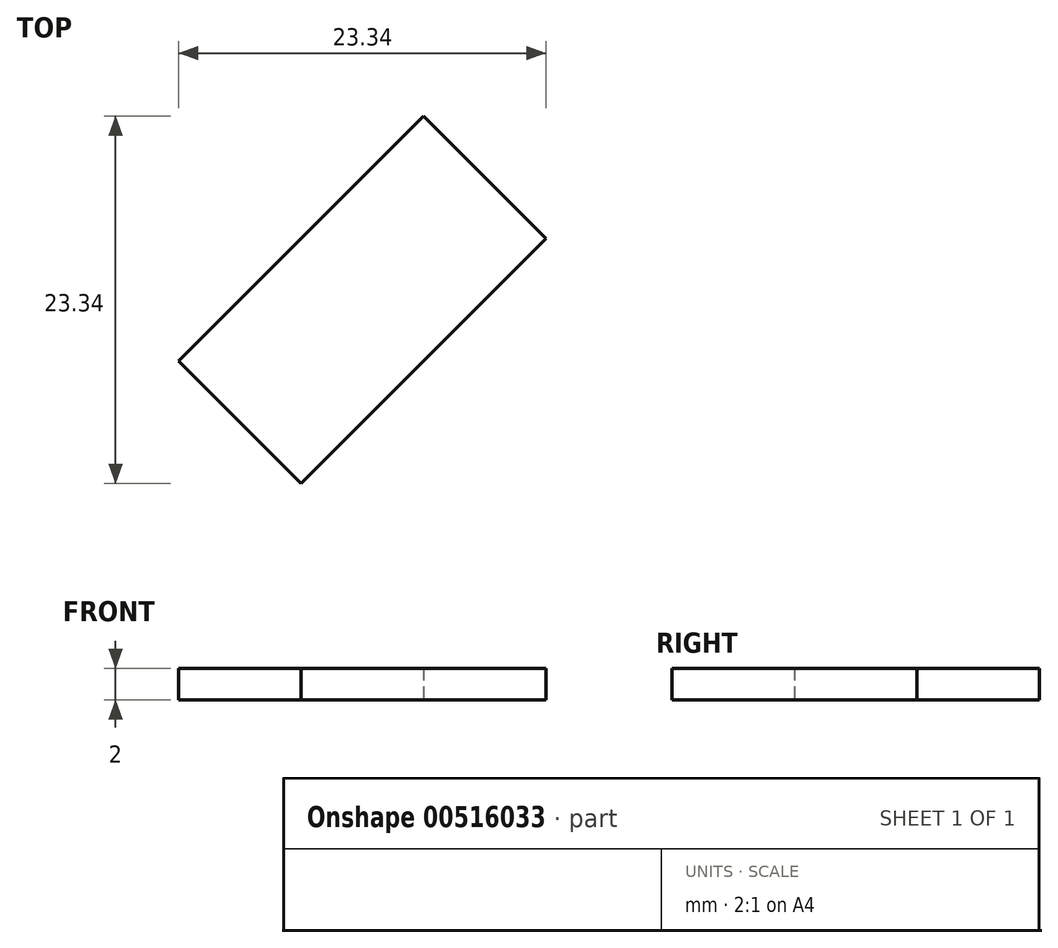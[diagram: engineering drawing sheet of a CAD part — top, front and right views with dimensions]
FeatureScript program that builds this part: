
annotation { "Feature Type Name" : "Feature", "Feature Type Description" : "" }
export const myFeature = defineFeature(function(context is Context, id is Id, definition is map)
    precondition{}
    {
        {
            var Q0;
            Q0=qCreatedBy(makeId("Top.planeOp"),FACE);
            var sketch = newSketch(context, id + "F0", { "sketchPlane" : qUnion([Q0])});
            skLineSegment(sketch, "E0", {"start": v(-7.78, 0) * mm, "end": v(0, -7.78) * mm});
            skLineSegment(sketch, "E1", {"start": v(0, -7.78) * mm, "end": v(15.56, 7.78) * mm});
            skLineSegment(sketch, "E2", {"start": v(15.56, 7.78) * mm, "end": v(7.78, 15.56) * mm});
            skLineSegment(sketch, "E3", {"start": v(7.78, 15.56) * mm, "end": v(-7.78, 0) * mm});
            skSolve(sketch);
        }
        {
            var Q0;
            Q0 = qSketchRegion(id + "F0", true);
            extrude(context, id + "F1", {"entities" : qUnion([Q0]), "depth" : 2 * mm, "offsetDistance" : 25 * mm});
        }
    });
